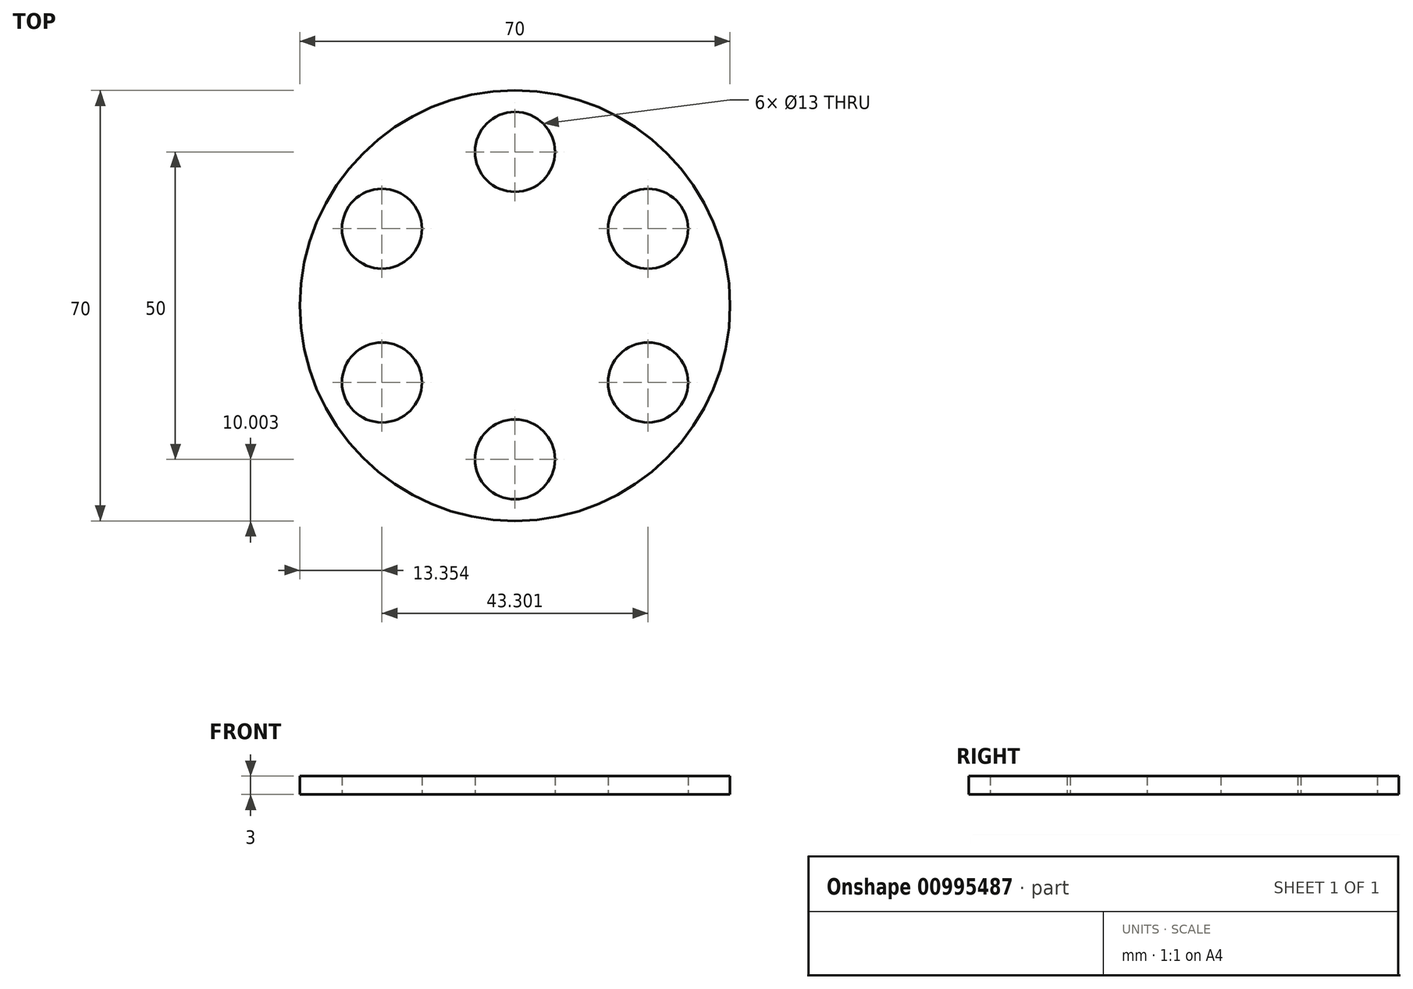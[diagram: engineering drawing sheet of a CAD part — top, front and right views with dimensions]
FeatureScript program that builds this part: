
annotation { "Feature Type Name" : "Feature", "Feature Type Description" : "" }
export const myFeature = defineFeature(function(context is Context, id is Id, definition is map)
    precondition{}
    {
        {
            var Q0;
            Q0=qCreatedBy(makeId("Top.planeOp"),FACE);
            var sketch = newSketch(context, id + "F0", { "sketchPlane" : qUnion([Q0])});
            skLineSegment(sketch, "E0", {"start": v(0.41, -0.09) * mm, "end": v(0.41, 18.41) * mm});
            skLineSegment(sketch, "E1", {"start": v(0.41, -0.09) * mm, "end": v(0.41, -18.59) * mm});
            skCircle(sketch, "E2", {"center": v(0.41, 24.91) * mm, "radius": 6.5 * mm});
            skCircle(sketch, "E3.1.0", {"center": v(-21.24, 12.41) * mm, "radius": 6.5 * mm});
            skCircle(sketch, "E3.2.0", {"center": v(-21.24, -12.59) * mm, "radius": 6.5 * mm});
            skCircle(sketch, "E3.3.0", {"center": v(0.41, -25.09) * mm, "radius": 6.5 * mm});
            skCircle(sketch, "E3.4.0", {"center": v(22.07, -12.59) * mm, "radius": 6.5 * mm});
            skCircle(sketch, "E3.5.0", {"center": v(22.07, 12.41) * mm, "radius": 6.5 * mm});
            skLineSegment(sketch, "E4", {"start": v(0.41, -0.09) * mm, "end": v(22.07, -12.59) * mm});
            skLineSegment(sketch, "E5", {"start": v(0.41, -0.09) * mm, "end": v(22.07, 12.41) * mm});
            skLineSegment(sketch, "E6", {"start": v(-21.24, 12.41) * mm, "end": v(0.41, -0.09) * mm});
            skLineSegment(sketch, "E7", {"start": v(-21.24, -12.59) * mm, "end": v(0.41, -0.09) * mm});
            skCircle(sketch, "E8", {"center": v(0.41, -0.09) * mm, "radius": 35 * mm});
            skSolve(sketch);
        }
        {
            var Q0;
            Q0=makeQuery(id+"F0.imprint","IMPRINT",FACE,{"disambiguationData":[TD([[makeQuery(id+"F0.imprint","IMPRINT",EDGE,{"derivedFrom":sQuery(id+"F0.wireOp",EDGE,"E2")}),-1.0]])]});
            extrude(context, id + "F1", {"entities" : qUnion([Q0]), "depth" : 3 * mm, "offsetDistance" : 25 * mm});
        }
    });
